# Revit family: ISM_THERMIC_WS-B1000_z_bezposrednim_wyjsciem_wody_zimnej_modulem_ogrzewania_podlogowego_7zaworow
name_source: partatom
category: Mechanical Equipment
revit_build: Autodesk Revit 2017 (Build: 20160225_1515(x64)
units: mm (PartAtom-declared; Revit-internal decimal feet)

## family parameters
Always vertical = Yes
Cut with Voids When Loaded = No
Part Type = Normal
Room Calculation Point = No
Round Connector Dimension = Use Diameter
Shared = No
Work Plane-Based = No

## types (1)
- 7x
    Body Material 1 = Nickel_Coated_Brass
    Body Material 2 = Brass
    Body Material 3 = Plastic_White
    Body Material 4 = Copper_Plated
    Body Material 5 = Nickel_Coated_Brass
    Body Material 6 = Plastic_Light_Gray
    Body Material 7 = Steel
    Body Material 8 = Plastic_Green
    Body Material 9 = Polypropylene
    Flow1 = 0.0 L/s
    Flow2 = 0.0 L/s
    Flow3 = 0.0 L/s
    Flow4 = 0.0 L/s
    Flow5 = 0.0 L/s
    Flow6 = 0.0 L/s
    Flow7 = 0.0 L/s
    Manufacturer = Thermic
    Nominal Diameter 1 = 20 mm
    Nominal Diameter 2 = 20 mm
    Nominal Diameter 3 = 20 mm
    Nominal Diameter 4 = 20 mm
    Nominal Diameter 5 = 20 mm
    Nominal Diameter 6 = 20 mm
    Nominal Diameter 7 = 20 mm
    Type Comments = ISM THERMIC WS-B1000 z bezpośrednim wyjściem wody zimnej, modułem ogrzewania podłogowego, 7 zaworów
    URL = www.thermic.pl

## geometry (parser evidence)
native form markers: Sweep x3
no freeform markers — native parametric forms only
